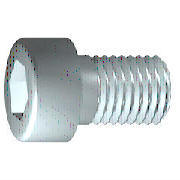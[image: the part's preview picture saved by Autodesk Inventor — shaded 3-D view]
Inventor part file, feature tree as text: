
AUTODESK INVENTOR PART (.ipt)
format: ipt  version: 2013 (Build 170138000, 138)  size: 176,640 bytes
history: native  units: mm (DEFAULTED — no unit token found)
features: sketch x2, extrude x1, plane x1, fillet x1
ambient origin geometry x7: Origin, YZ Plane, XY Plane, X Axis, Y Axis, Z Axis, Center Point
bodies: Solid1 (feature_tree), Body (feature_tree)
feature tree (5):
  extrude  "Slot"  Depth=0.766912mm
  plane  "Work Plane1"
  fillet  "Fillet2"  Radius=8.0mm
  sketch  "Sketch1"  dims[d1=28.0mm d2=0.766912mm d3=8.0mm]
  sketch  "Sketch2"  dims[d4=4.0mm d5=60.0deg d6=8.0mm d7=8.0mm d8=6.928203mm d9=13.0mm d10=90.0deg d11=10.0mm d12=0.0mm d13=28.0mm d14=0.0mm d15=0.766812mm d16=0.766813mm d17=0.8mm d19=0.0mm d26=160.0mm d27=45.0deg d28=0.0mm d29=0.0mm d30=0.1mm]
